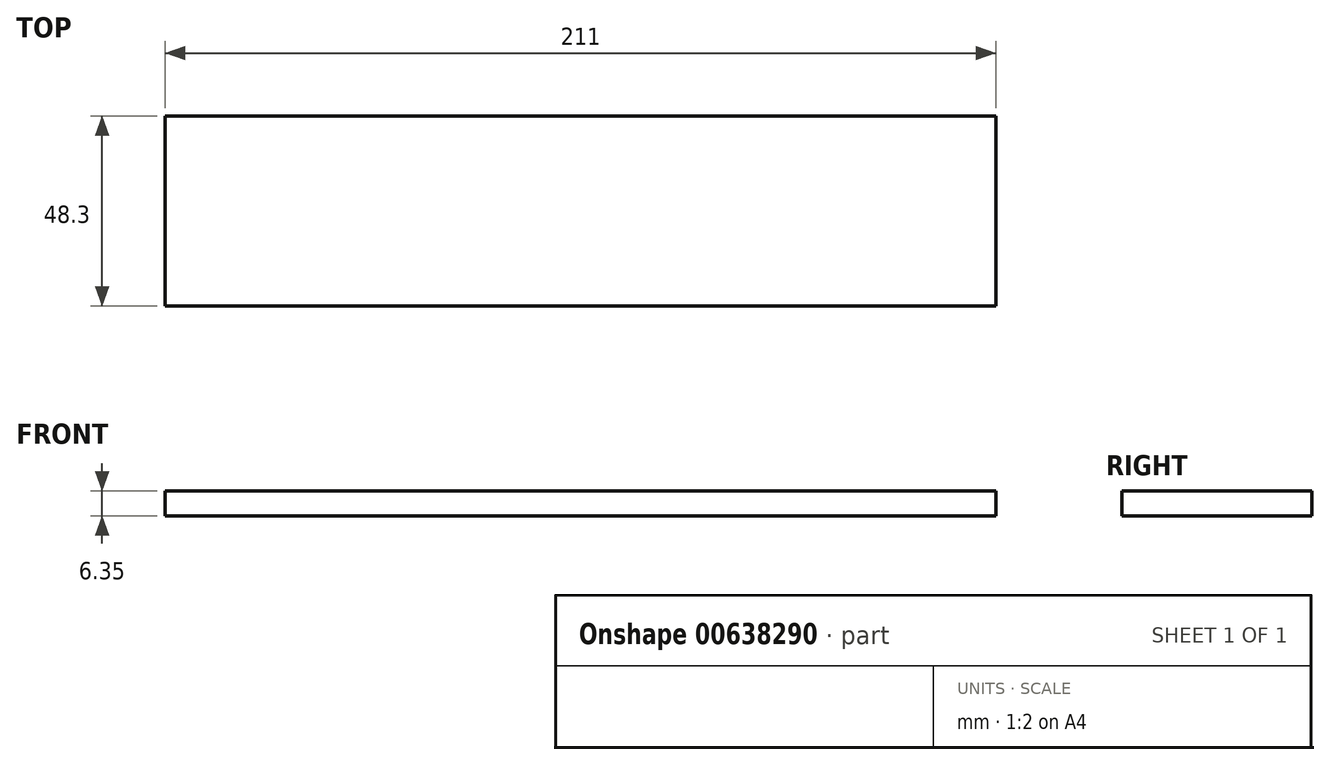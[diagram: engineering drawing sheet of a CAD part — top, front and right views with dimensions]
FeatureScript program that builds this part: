
annotation { "Feature Type Name" : "Feature", "Feature Type Description" : "" }
export const myFeature = defineFeature(function(context is Context, id is Id, definition is map)
    precondition{}
    {
        {
            var Q0;
            Q0=qCreatedBy(makeId("Top.planeOp"),FACE);
            var sketch = newSketch(context, id + "F0", { "sketchPlane" : qUnion([Q0])});
            skLineSegment(sketch, "E0.bottom", {"start": v(0, 0) * mm, "end": v(211, 0) * mm});
            skLineSegment(sketch, "E0.top", {"start": v(0, -48.3) * mm, "end": v(211, -48.3) * mm});
            skLineSegment(sketch, "E0.left", {"start": v(0, 0) * mm, "end": v(0, -48.3) * mm});
            skLineSegment(sketch, "E0.right", {"start": v(211, 0) * mm, "end": v(211, -48.3) * mm});
            skSolve(sketch);
        }
        {
            var Q0;
            Q0=makeQuery(id+"F0.imprint","IMPRINT",FACE,{"disambiguationData":[TD([[makeQuery(id+"F0.imprint","IMPRINT",EDGE,{"derivedFrom":sQuery(id+"F0.wireOp",EDGE,"E0.bottom")}),-1.0]])]});
            extrude(context, id + "F1", {"entities" : qUnion([Q0]), "depth" : 6.35 * mm, "offsetDistance" : 25.4 * mm});
        }
    });
